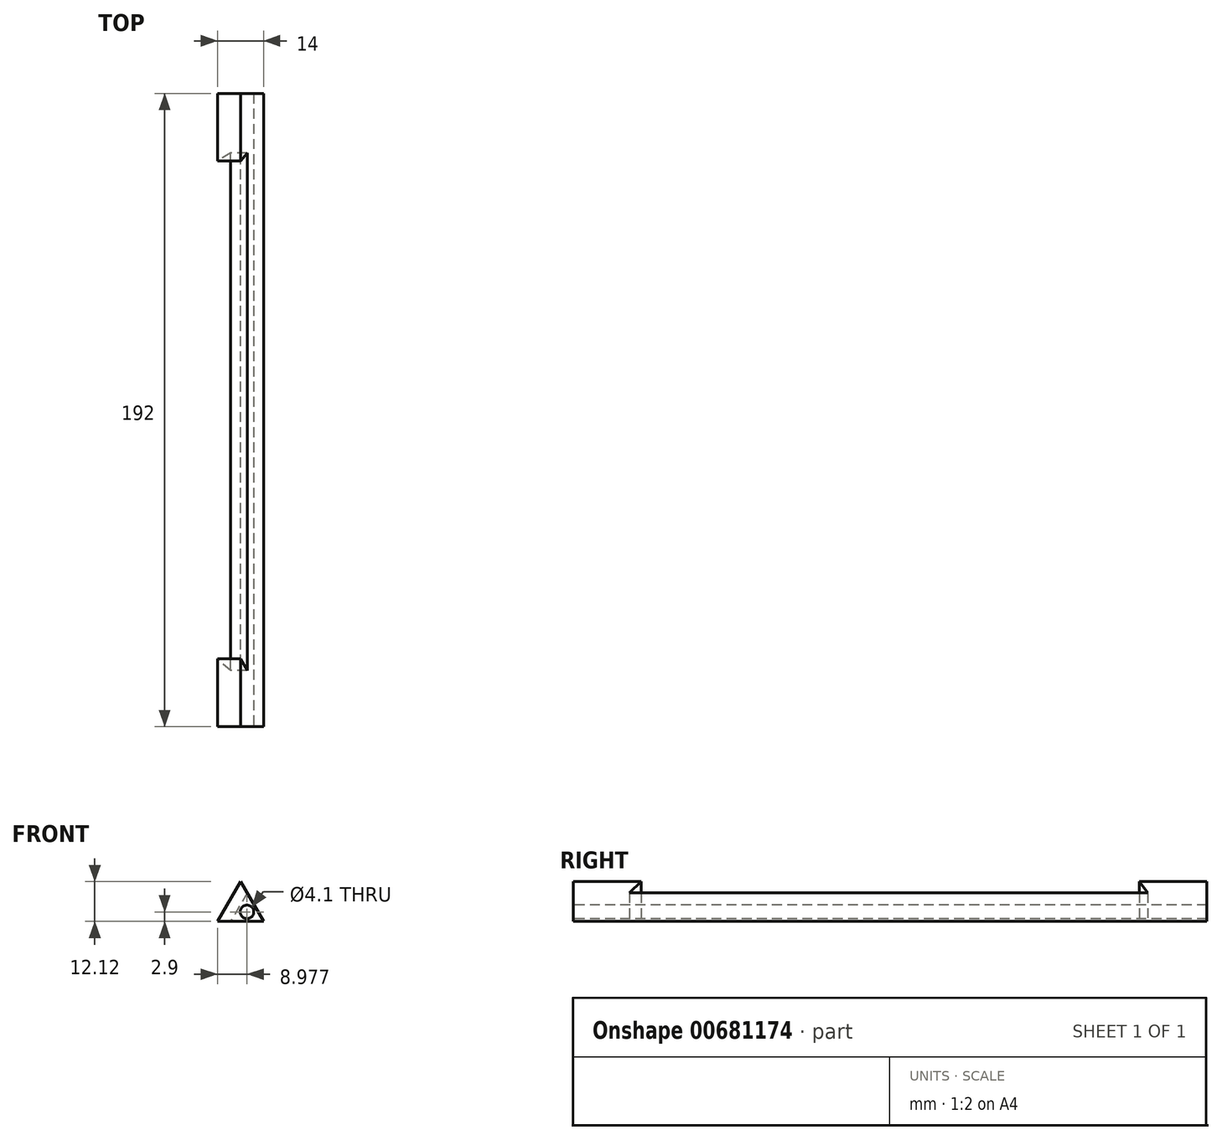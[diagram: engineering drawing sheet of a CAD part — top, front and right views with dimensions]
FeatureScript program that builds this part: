
annotation { "Feature Type Name" : "Feature", "Feature Type Description" : "" }
export const myFeature = defineFeature(function(context is Context, id is Id, definition is map)
    precondition{}
    {
        {
            var Q0;
            Q0=qCreatedBy(makeId("Front.planeOp"),FACE);
            var sketch = newSketch(context, id + "F0", { "sketchPlane" : qUnion([Q0])});
            skLineSegment(sketch, "E0", {"start": v(-7, 0) * mm, "end": v(7, 0) * mm});
            skLineSegment(sketch, "E1", {"start": v(7, 0) * mm, "end": v(0, 12.12) * mm});
            skLineSegment(sketch, "E2", {"start": v(0, 12.12) * mm, "end": v(-7, 0) * mm});
            skSolve(sketch);
        }
        {
            var Q0;
            Q0=makeQuery(id+"F0.imprint","IMPRINT",FACE,{"disambiguationData":[TD([[makeQuery(id+"F0.imprint","IMPRINT",EDGE,{"derivedFrom":sQuery(id+"F0.wireOp",EDGE,"E0")}),1.0]])]});
            extrude(context, id + "F1", {"entities" : qUnion([Q0]), "oppositeDirection" : true, "depth" : 192 * mm, "offsetDistance" : 25 * mm});
        }
        {
            var Q0;
            Q0=makeQuery(id+"F1.opExtrude","CAP_EDGE",EDGE,{"disambiguationData":[OSD([sQuery(id+"F0.wireOp",EDGE,"E2")])],"isStart":false});
            cPoint(context, id + "F2", {"entities" : qUnion([Q0]), "parameter" : 0.5});
        }
        {
            var Q0;
            Q0=makeQuery(id+"F1.opExtrude","CAP_VERTEX",VERTEX,{"disambiguationData":[OSD([sQuery(id+"F0.wireOp",EDGE,"E0"),sQuery(id+"F0.wireOp",EDGE,"E1")])],"isStart":false});
            var Q1;
            Q1=makeQuery(id+"F1.opExtrude","CAP_VERTEX",VERTEX,{"disambiguationData":[OSD([sQuery(id+"F0.wireOp",EDGE,"E0"),sQuery(id+"F0.wireOp",EDGE,"E1")])],"isStart":true});
            var Q2;
            Q2 = qCreatedBy(id + "F2" ,VERTEX);
            cPlane(context, id + "F3", {"entities" : qUnion([Q0, Q1, Q2]), "cplaneType" : CPlaneType.THREE_POINT, "offset" : 25 * mm, "width" : 150 * mm, "height" : 150 * mm});
        }
        {
            var Q0;
            Q0=qCreatedBy(id+"F3.planeOp",FACE);
            var sketch = newSketch(context, id + "F4", { "sketchPlane" : qUnion([Q0])});
            skLineSegment(sketch, "E3", {"start": v(-2.56, 17) * mm, "end": v(-2.56, 174) * mm});
            skLineSegment(sketch, "E4", {"start": v(-2.56, 174) * mm, "end": v(-6.06, 171.5) * mm});
            skLineSegment(sketch, "E5", {"start": v(-6.06, 171.5) * mm, "end": v(-6.06, 20.5) * mm});
            skLineSegment(sketch, "E6", {"start": v(-2.56, 17) * mm, "end": v(-6.06, 20.5) * mm});
            skSolve(sketch);
        }
        {
            var Q0;
            Q0 = qSketchRegion(id + "F4", true);
            extrude(context, id + "F5", {"entities" : qUnion([Q0]), "operationType" : NewBodyOperationType.REMOVE, "endBound" : BoundingType.SYMMETRIC, "depth" : 25 * mm, "offsetDistance" : 25 * mm});
        }
        {
            var Q0;
            Q0=qCreatedBy(makeId("Front.planeOp"),FACE);
            var sketch = newSketch(context, id + "F6", { "sketchPlane" : qUnion([Q0])});
            skCircle(sketch, "E7", {"center": v(1.98, 2.9) * mm, "radius": 2.05 * mm});
            skSolve(sketch);
        }
        {
            var Q0;
            Q0=makeQuery(id+"F6.imprint","IMPRINT",FACE,{"disambiguationData":[TD([[makeQuery(id+"F6.imprint","IMPRINT",EDGE,{"derivedFrom":sQuery(id+"F6.wireOp",EDGE,"E7")}),1.0]])]});
            extrude(context, id + "F7", {"entities" : qUnion([Q0]), "operationType" : NewBodyOperationType.REMOVE, "oppositeDirection" : true, "depth" : 200 * mm, "offsetDistance" : 25 * mm});
        }
    });
